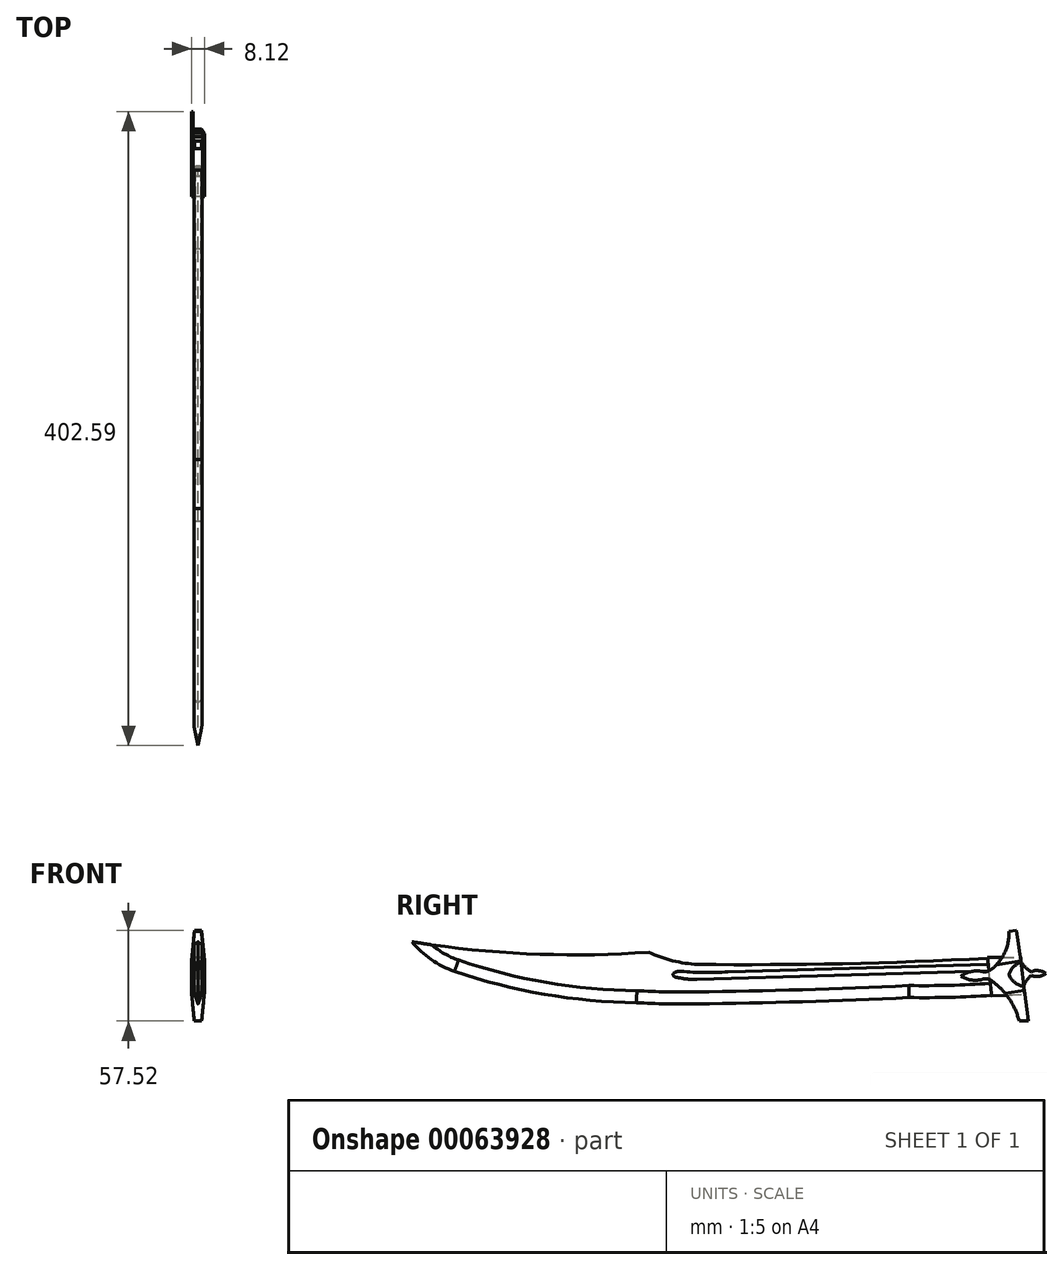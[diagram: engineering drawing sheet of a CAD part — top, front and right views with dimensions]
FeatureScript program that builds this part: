
annotation { "Feature Type Name" : "Feature", "Feature Type Description" : "" }
export const myFeature = defineFeature(function(context is Context, id is Id, definition is map)
    precondition{}
    {
        {
            var Q0;
            Q0=qCreatedBy(makeId("Right.planeOp"),FACE);
            var sketch = newSketch(context, id + "F0", { "sketchPlane" : qUnion([Q0])});
            skArc(sketch, "E0", {"start": v(-222.62, 23.87) * mm, "mid": v(-147.62, 16.22) * mm, "end": v(-72.23, 17.25) * mm});
            skArc(sketch, "E1", {"start": v(-72.23, 17.25) * mm, "mid": v(-57.05, 11.87) * mm, "end": v(-41.12, 9.52) * mm});
            skArc(sketch, "E2", {"start": v(-41.12, 9.52) * mm, "mid": v(50.92, 9.98) * mm, "end": v(142.9, 13.44) * mm});
            skArc(sketch, "E3", {"start": v(-222.62, 23.87) * mm, "mid": v(-210.4, 12.6) * mm, "end": v(-195.6, 5.02) * mm});
            skArc(sketch, "E4", {"start": v(-195.6, 5.02) * mm, "mid": v(-138.62, -9.45) * mm, "end": v(-80.08, -14.85) * mm});
            skLineSegment(sketch, "E5", {"start": v(145.39, -10.22) * mm, "end": v(142.9, 13.44) * mm});
            skArc(sketch, "E6", {"start": v(-80.08, -14.85) * mm, "mid": v(-61.15, -15.54) * mm, "end": v(-42.22, -15.5) * mm});
            skArc(sketch, "E7", {"start": v(-42.22, -15.5) * mm, "mid": v(25.43, -14.14) * mm, "end": v(93.04, -11.56) * mm});
            skArc(sketch, "E8", {"start": v(93.04, -11.56) * mm, "mid": v(119.22, -11.4) * mm, "end": v(145.39, -10.22) * mm});
            skSolve(sketch);
        }
        {
            var Q0;
            Q0 = qSketchRegion(id + "F0", true);
            extrude(context, id + "F1", {"entities" : qUnion([Q0]), "endBound" : BoundingType.SYMMETRIC, "depth" : 5.08 * mm});
        }
        {
            var Q0;
            Q0=qCreatedBy(makeId("Right.planeOp"),FACE);
            var sketch = newSketch(context, id + "F2", { "sketchPlane" : qUnion([Q0])});
            skLineSegment(sketch, "E9.0", {"start": v(145.39, -10.22) * mm, "end": v(142.9, 13.44) * mm});
            skLineSegment(sketch, "E10", {"start": v(143.75, 5.38) * mm, "end": v(-41.72, 0) * mm});
            skLineSegment(sketch, "E11", {"start": v(143.31, 9.5) * mm, "end": v(-22.07, 4.7) * mm});
            skPoint(sketch, "E12", {"position": v(-38, 4.24) * mm});
            skPoint(sketch, "E13.orphan", {"position": v(-55.48, 4.24) * mm});
            skPoint(sketch, "E14.start.orphan", {"position": v(-40.81, 4.24) * mm});
            skArc(sketch, "E15", {"start": v(-51.64, 5.05) * mm, "mid": v(-36.86, 4.37) * mm, "end": v(-22.07, 4.7) * mm});
            skArc(sketch, "E16", {"start": v(-53.43, 1.1) * mm, "mid": v(-47.61, 0.19) * mm, "end": v(-41.72, 0) * mm});
            skLineSegment(sketch, "E17", {"start": v(-52.54, 3.07) * mm, "end": v(-53.43, 1.1) * mm});
            skEllipticalArc(sketch, "E18", {});
            const initialGuessF2  = {"E18": [-0.05253797210752964, 0.0030729959253221716, -1, 0, 0.004336996003985405, 0.0020197694829036552, 4.504185753460669, 1.3625930998708757]};
            skSetInitialGuess(sketch, initialGuessF2);
            skSolve(sketch);
        }
        {
            var Q0;
            Q0=makeQuery(id+"F1.opExtrude","CAP_FACE",FACE,{"disambiguationData":[OSD([sQuery(id+"F0.wireOp",EDGE,"E0"),sQuery(id+"F0.wireOp",EDGE,"E1"),sQuery(id+"F0.wireOp",EDGE,"E2"),sQuery(id+"F0.wireOp",EDGE,"E3"),sQuery(id+"F0.wireOp",EDGE,"E4"),sQuery(id+"F0.wireOp",EDGE,"E5"),sQuery(id+"F0.wireOp",EDGE,"E6"),sQuery(id+"F0.wireOp",EDGE,"E7"),sQuery(id+"F0.wireOp",EDGE,"E8")])],"isStart":false});
            var sketch = newSketch(context, id + "F3", { "sketchPlane" : qUnion([Q0])});
            skEllipticalArc(sketch, "E19.0", {});
            skArc(sketch, "E20.0", {"start": v(-53.43, 1.1) * mm, "mid": v(-47.61, 0.19) * mm, "end": v(-41.72, 0) * mm});
            skLineSegment(sketch, "E21.0", {"start": v(143.75, 5.38) * mm, "end": v(-41.72, 0) * mm});
            skArc(sketch, "E22.0", {"start": v(-51.64, 5.05) * mm, "mid": v(-36.86, 4.37) * mm, "end": v(-22.07, 4.7) * mm});
            skLineSegment(sketch, "E23.0", {"start": v(143.31, 9.5) * mm, "end": v(-22.07, 4.7) * mm});
            skLineSegment(sketch, "E24.0", {"start": v(145.39, -10.22) * mm, "end": v(142.9, 13.44) * mm});
            const initialGuessF3  = {"E19.0": [-0.05253797210752964, 0.0030729959253221716, -1, 0, 0.004336996003985405, 0.0020197694829036552, 4.504185753460669, 1.3625930998708757]};
            skSetInitialGuess(sketch, initialGuessF3);
            skSolve(sketch);
        }
        {
            var Q0;
            Q0 = qSketchRegion(id + "F3", true);
            extrude(context, id + "F4", {"entities" : qUnion([Q0]), "operationType" : NewBodyOperationType.REMOVE, "oppositeDirection" : true, "depth" : 0.76 * mm});
        }
        {
            var Q0;
            Q0=makeQuery(id+"F1.opExtrude","CAP_FACE",FACE,{"disambiguationData":[OSD([sQuery(id+"F0.wireOp",EDGE,"E0"),sQuery(id+"F0.wireOp",EDGE,"E1"),sQuery(id+"F0.wireOp",EDGE,"E2"),sQuery(id+"F0.wireOp",EDGE,"E3"),sQuery(id+"F0.wireOp",EDGE,"E4"),sQuery(id+"F0.wireOp",EDGE,"E5"),sQuery(id+"F0.wireOp",EDGE,"E6"),sQuery(id+"F0.wireOp",EDGE,"E7"),sQuery(id+"F0.wireOp",EDGE,"E8")])],"isStart":true});
            var sketch = newSketch(context, id + "F5", { "sketchPlane" : qUnion([Q0])});
            skArc(sketch, "E25.0", {"start": v(53.43, 1.1) * mm, "mid": v(47.61, 0.19) * mm, "end": v(41.72, 0) * mm});
            skLineSegment(sketch, "E26.0", {"start": v(-143.75, 5.38) * mm, "end": v(41.72, 0) * mm});
            skEllipticalArc(sketch, "E27.0", {});
            skArc(sketch, "E28.0", {"start": v(51.64, 5.05) * mm, "mid": v(36.86, 4.37) * mm, "end": v(22.07, 4.7) * mm});
            skLineSegment(sketch, "E29.0", {"start": v(-143.31, 9.5) * mm, "end": v(22.07, 4.7) * mm});
            skLineSegment(sketch, "E30.0", {"start": v(-145.39, -10.22) * mm, "end": v(-142.9, 13.44) * mm});
            const initialGuessF5  = {"E27.0": [0.05253797210752964, 0.0030729959253221716, 1, 0, 0.004336996003985405, 0.0020197694829036552, 4.920592207308711, 1.7789995537189176]};
            skSetInitialGuess(sketch, initialGuessF5);
            skSolve(sketch);
        }
        {
            var Q0;
            Q0 = qSketchRegion(id + "F5", true);
            extrude(context, id + "F6", {"entities" : qUnion([Q0]), "operationType" : NewBodyOperationType.REMOVE, "oppositeDirection" : true, "depth" : 0.76 * mm});
        }
        {
            var Q0;
            Q0=makeQuery(id+"F1.opExtrude","CAP_EDGE",EDGE,{"disambiguationData":[OSD([sQuery(id+"F0.wireOp",EDGE,"E4")])],"isStart":false});
            var Q1;
            Q1=makeQuery(id+"F1.opExtrude","CAP_EDGE",EDGE,{"disambiguationData":[OSD([sQuery(id+"F0.wireOp",EDGE,"E6")])],"isStart":false});
            var Q2;
            Q2=makeQuery(id+"F1.opExtrude","CAP_EDGE",EDGE,{"disambiguationData":[OSD([sQuery(id+"F0.wireOp",EDGE,"E7")])],"isStart":false});
            var Q3;
            Q3=makeQuery(id+"F1.opExtrude","CAP_EDGE",EDGE,{"disambiguationData":[OSD([sQuery(id+"F0.wireOp",EDGE,"E8")])],"isStart":false});
            var Q4;
            Q4=makeQuery(id+"F1.opExtrude","CAP_EDGE",EDGE,{"disambiguationData":[OSD([sQuery(id+"F0.wireOp",EDGE,"E3")])],"isStart":false});
            chamfer(context, id + "F7", {"entities" : qUnion([Q0, Q1, Q2, Q3, Q4]), "chamferType" : ChamferType.TWO_OFFSETS, "width1" : 7.62 * mm, "oppositeDirection" : false, "width2" : 2.54 * mm, "tangentPropagation" : true});
        }
        {
            var Q0;
            Q0=makeQuery(id+"F1.opExtrude","CAP_EDGE",EDGE,{"disambiguationData":[OSD([sQuery(id+"F0.wireOp",EDGE,"E4")])],"isStart":true});
            var Q1;
            Q1=makeQuery(id+"F1.opExtrude","CAP_EDGE",EDGE,{"disambiguationData":[OSD([sQuery(id+"F0.wireOp",EDGE,"E3")])],"isStart":true});
            var Q2;
            Q2=makeQuery(id+"F1.opExtrude","CAP_EDGE",EDGE,{"disambiguationData":[OSD([sQuery(id+"F0.wireOp",EDGE,"E6")])],"isStart":true});
            var Q3;
            Q3=makeQuery(id+"F1.opExtrude","CAP_EDGE",EDGE,{"disambiguationData":[OSD([sQuery(id+"F0.wireOp",EDGE,"E7")])],"isStart":true});
            var Q4;
            Q4=makeQuery(id+"F1.opExtrude","CAP_EDGE",EDGE,{"disambiguationData":[OSD([sQuery(id+"F0.wireOp",EDGE,"E8")])],"isStart":true});
            chamfer(context, id + "F8", {"entities" : qUnion([Q0, Q1, Q2, Q3, Q4]), "chamferType" : ChamferType.TWO_OFFSETS, "width1" : 2.54 * mm, "oppositeDirection" : false, "width2" : 7.62 * mm, "tangentPropagation" : true});
        }
        {
            var Q0;
            Q0=qCreatedBy(makeId("Right.planeOp"),FACE);
            var sketch = newSketch(context, id + "F9", { "sketchPlane" : qUnion([Q0])});
            skLineSegment(sketch, "E31.0", {"start": v(145.39, -10.22) * mm, "end": v(142.9, 13.44) * mm});
            skLineSegment(sketch, "E32", {"start": v(142.9, 13.44) * mm, "end": v(142.84, 13.99) * mm});
            skLineSegment(sketch, "E33", {"start": v(145.39, -10.22) * mm, "end": v(145.42, -10.53) * mm});
            skLineSegment(sketch, "E34", {"start": v(145.42, -10.53) * mm, "end": v(166.56, -9.44) * mm});
            skLineSegment(sketch, "E35", {"start": v(142.84, 13.99) * mm, "end": v(164.01, 13.99) * mm});
            skLineSegment(sketch, "E36", {"start": v(164.01, 13.99) * mm, "end": v(166.56, -9.44) * mm});
            skSolve(sketch);
        }
        {
            var Q0;
            Q0 = qSketchRegion(id + "F9", true);
            extrude(context, id + "F10", {"entities" : qUnion([Q0]), "endBound" : BoundingType.SYMMETRIC, "depth" : 6.1 * mm});
        }
        {
            var Q0;
            Q0=makeQuery(id+"F10.opExtrude","CAP_EDGE",EDGE,{"disambiguationData":[OSD([sQuery(id+"F9.wireOp",EDGE,"E35")])],"isStart":false});
            var Q1;
            Q1=makeQuery(id+"F10.opExtrude","CAP_EDGE",EDGE,{"disambiguationData":[OSD([sQuery(id+"F9.wireOp",EDGE,"E35")])],"isStart":true});
            var Q2;
            Q2=makeQuery(id+"F10.opExtrude","CAP_EDGE",EDGE,{"disambiguationData":[OSD([sQuery(id+"F9.wireOp",EDGE,"E34")])],"isStart":false});
            var Q3;
            Q3=makeQuery(id+"F10.opExtrude","CAP_EDGE",EDGE,{"disambiguationData":[OSD([sQuery(id+"F9.wireOp",EDGE,"E34")])],"isStart":true});
            fillet(context, id + "F11", {"entities" : qUnion([Q0, Q1, Q2, Q3]), "radius" : 1.78 * mm, "tangentPropagation" : true, "allowEdgeOverflow" : false});
        }
        {
            var Q0;
            Q0=qCreatedBy(makeId("Right.planeOp"),FACE);
            var sketch = newSketch(context, id + "F12", { "sketchPlane" : qUnion([Q0])});
            skArc(sketch, "E37", {"start": v(138.74, 5.21) * mm, "mid": v(141.56, 4.82) * mm, "end": v(144.29, 5.6) * mm});
            skArc(sketch, "E38", {"start": v(138.74, 5.21) * mm, "mid": v(132.09, 4.9) * mm, "end": v(126.06, 2.05) * mm});
            skLineSegment(sketch, "E39.0", {"start": v(145.39, -10.22) * mm, "end": v(142.9, 13.44) * mm});
            skLineSegment(sketch, "E40", {"start": v(155.65, 31.05) * mm, "end": v(161.25, 31.05) * mm});
            skLineSegment(sketch, "E41", {"start": v(161.25, 31.05) * mm, "end": v(164.28, 10.92) * mm});
            skArc(sketch, "E42", {"start": v(164.28, 10.92) * mm, "mid": v(159.47, 7.98) * mm, "end": v(156.53, 3.17) * mm});
            skLineSegment(sketch, "E43", {"start": v(156.53, 3.17) * mm, "end": v(126.06, 2.05) * mm});
            skArc(sketch, "E44.MirrorCS", {"start": v(138.94, -0.18) * mm, "mid": v(132.28, -0.34) * mm, "end": v(126.06, 2.05) * mm});
            skArc(sketch, "E45.MirrorCS", {"start": v(138.94, -0.18) * mm, "mid": v(141.72, 0.43) * mm, "end": v(144.5, -0.15) * mm});
            skArc(sketch, "E46", {"start": v(163.03, -26.47) * mm, "mid": v(156.17, -11.62) * mm, "end": v(144.5, -0.15) * mm});
            skArc(sketch, "E47", {"start": v(156.53, 3.17) * mm, "mid": v(160.14, -1.89) * mm, "end": v(165.82, -4.38) * mm});
            skLineSegment(sketch, "E48", {"start": v(163.03, -26.47) * mm, "end": v(168.8, -26.47) * mm});
            skLineSegment(sketch, "E49", {"start": v(168.8, -26.47) * mm, "end": v(165.82, -4.38) * mm});
            skArc(sketch, "E50", {"start": v(144.29, 5.6) * mm, "mid": v(153.74, 16.72) * mm, "end": v(156.48, 31.05) * mm});
            skSolve(sketch);
        }
        {
            var Q0;
            Q0 = qSketchRegion(id + "F12", true);
            extrude(context, id + "F13", {"entities" : qUnion([Q0]), "endBound" : BoundingType.SYMMETRIC, "depth" : 8.13 * mm});
        }
        {
            var Q0;
            Q0=makeQuery(id+"F13.opExtrude","CAP_EDGE",EDGE,{"disambiguationData":[OSD([sQuery(id+"F12.wireOp",EDGE,"E42")])],"isStart":false});
            var Q1;
            Q1=makeQuery(id+"F13.opExtrude","CAP_EDGE",EDGE,{"disambiguationData":[OSD([sQuery(id+"F12.wireOp",EDGE,"E47")])],"isStart":false});
            var Q2;
            Q2=makeQuery(id+"F13.opExtrude","CAP_EDGE",EDGE,{"disambiguationData":[OSD([sQuery(id+"F12.wireOp",EDGE,"E42")])],"isStart":true});
            var Q3;
            Q3=makeQuery(id+"F13.opExtrude","CAP_EDGE",EDGE,{"disambiguationData":[OSD([sQuery(id+"F12.wireOp",EDGE,"E47")])],"isStart":true});
            fillet(context, id + "F14", {"entities" : qUnion([Q0, Q1, Q2, Q3]), "radius" : 0.76 * mm, "tangentPropagation" : true, "allowEdgeOverflow" : false});
        }
        {
            var Q0;
            Q0=makeQuery(id+"F13.opExtrude","SWEPT_FACE",FACE,{"disambiguationData":[OSD([sQuery(id+"F12.wireOp",EDGE,"E41")])]});
            var sketch = newSketch(context, id + "F15", { "sketchPlane" : qUnion([Q0])});
            skLineSegment(sketch, "E51", {"start": v(-4.06, -12.88) * mm, "end": v(-2.27, 6.7) * mm});
            skPoint(sketch, "E52.start.orphan", {"position": v(0, -25.1) * mm});
            skLineSegment(sketch, "E53", {"start": v(0, -24.7) * mm, "end": v(0, -24.57) * mm});
            skLineSegment(sketch, "E54", {"start": v(0, -24.57) * mm, "end": v(0, -24.7) * mm});
            skLineSegment(sketch, "E55", {"start": v(0, -24.7) * mm, "end": v(-0.45, -24.7) * mm});
            skLineSegment(sketch, "E56", {"start": v(0, -24.57) * mm, "end": v(0, -23.61) * mm});
            skLineSegment(sketch, "E57.MirrorCS", {"start": v(4.06, -12.88) * mm, "end": v(2.27, 6.7) * mm});
            skLineSegment(sketch, "E58", {"start": v(-4.06, -12.88) * mm, "end": v(-14.59, -7) * mm});
            skLineSegment(sketch, "E59", {"start": v(-14.59, -7) * mm, "end": v(-4.7, 7.88) * mm});
            skLineSegment(sketch, "E60", {"start": v(-4.7, 7.88) * mm, "end": v(-2.27, 6.7) * mm});
            skLineSegment(sketch, "E61", {"start": v(2.27, 6.7) * mm, "end": v(6.24, 9.12) * mm});
            skLineSegment(sketch, "E62", {"start": v(6.24, 9.12) * mm, "end": v(7.63, -11.04) * mm});
            skLineSegment(sketch, "E63", {"start": v(7.63, -11.04) * mm, "end": v(4.06, -12.88) * mm});
            skLineSegment(sketch, "E64.0", {"start": v(-4.06, -51.3) * mm, "end": v(4.06, -51.3) * mm});
            skLineSegment(sketch, "E65", {"start": v(0, -51.3) * mm, "end": v(0, 6.7) * mm});
            skPoint(sketch, "E66", {"position": v(0, -22.3) * mm});
            skLineSegment(sketch, "E67", {"start": v(0, -22.3) * mm, "end": v(-2.36, -22.3) * mm});
            skLineSegment(sketch, "E68.MirrorCS", {"start": v(-4.06, -31.71) * mm, "end": v(-2.27, -51.3) * mm});
            skLineSegment(sketch, "E69.MirrorCS", {"start": v(4.06, -31.71) * mm, "end": v(2.27, -51.3) * mm});
            skLineSegment(sketch, "E70.MirrorCS", {"start": v(7.63, -33.56) * mm, "end": v(4.06, -31.71) * mm});
            skLineSegment(sketch, "E71.MirrorCS", {"start": v(6.24, -53.71) * mm, "end": v(7.63, -33.56) * mm});
            skLineSegment(sketch, "E72.MirrorCS", {"start": v(-4.06, -31.71) * mm, "end": v(-14.59, -37.59) * mm});
            skLineSegment(sketch, "E73.MirrorCS", {"start": v(-14.59, -37.59) * mm, "end": v(-4.7, -52.48) * mm});
            skLineSegment(sketch, "E74.MirrorCS", {"start": v(-4.7, -52.48) * mm, "end": v(-2.27, -51.3) * mm});
            skLineSegment(sketch, "E75.MirrorCS", {"start": v(2.27, -51.3) * mm, "end": v(6.24, -53.71) * mm});
            skLineSegment(sketch, "E76", {"start": v(-2.27, 6.7) * mm, "end": v(2.27, 6.7) * mm});
            skLineSegment(sketch, "E77", {"start": v(-2.27, 6.7) * mm, "end": v(-2.27, 10.48) * mm});
            skLineSegment(sketch, "E78", {"start": v(-2.27, 10.48) * mm, "end": v(-4.7, 7.88) * mm});
            skLineSegment(sketch, "E79", {"start": v(2.27, 6.7) * mm, "end": v(2.27, 12.28) * mm});
            skLineSegment(sketch, "E80", {"start": v(2.27, 12.28) * mm, "end": v(6.24, 9.12) * mm});
            skLineSegment(sketch, "E81", {"start": v(-2.27, 10.48) * mm, "end": v(2.27, 12.28) * mm});
            skSolve(sketch);
        }
        {
            var Q0;
            {var subQ0=sQuery(id+"F15.wireOp",EDGE,"E77");Q0=makeQuery(id+"F15.imprint","IMPRINT",FACE,{"disambiguationData":[TD([[makeQuery(id+"F15.imprint","IMPRINT",EDGE,{"derivedFrom":subQ0}),-1.0]])]});}
            var Q1;
            Q1=makeQuery(id+"F15.imprint","IMPRINT",FACE,{"disambiguationData":[TD([[makeQuery(id+"F15.imprint","IMPRINT",EDGE,{"derivedFrom":sQuery(id+"F15.wireOp",EDGE,"E61")}),1.0]])]});
            var Q2;
            Q2=makeQuery(id+"F15.imprint","IMPRINT",FACE,{"disambiguationData":[TD([[makeQuery(id+"F15.imprint","IMPRINT",EDGE,{"derivedFrom":sQuery(id+"F15.wireOp",EDGE,"E60")}),1.0]])]});
            var Q3;
            Q3=makeQuery(id+"F15.imprint","IMPRINT",FACE,{"disambiguationData":[TD([[makeQuery(id+"F15.imprint","IMPRINT",EDGE,{"derivedFrom":sQuery(id+"F15.wireOp",EDGE,"E58")}),-1.0]])]});
            var Q4;
            {var subQ2=sQuery(id+"F15.wireOp",EDGE,"E61");Q4=makeQuery(id+"F15.imprint","IMPRINT",FACE,{"disambiguationData":[TD([[makeQuery(id+"F15.imprint","IMPRINT",EDGE,{"derivedFrom":subQ2}),-1.0]])]});}
            var Q5;
            {var subQ0=sQuery(id+"F15.wireOp",EDGE,"E51");Q5=makeQuery(id+"F15.imprint","IMPRINT",FACE,{"disambiguationData":[TD([[makeQuery(id+"F15.imprint","IMPRINT",EDGE,{"derivedFrom":subQ0}),1.0]])]});}
            var Q6;
            {var subQ0=sQuery(id+"F15.wireOp",EDGE,"E57.MirrorCS");Q6=makeQuery(id+"F15.imprint","IMPRINT",FACE,{"disambiguationData":[TD([[makeQuery(id+"F15.imprint","IMPRINT",EDGE,{"derivedFrom":subQ0}),-1.0]])]});}
            var Q7;
            Q7=makeQuery(id+"F15.imprint","IMPRINT",FACE,{"disambiguationData":[TD([[makeQuery(id+"F15.imprint","IMPRINT",EDGE,{"derivedFrom":sQuery(id+"F15.wireOp",EDGE,"E68.MirrorCS")}),-1.0]])]});
            var Q8;
            Q8=makeQuery(id+"F15.imprint","IMPRINT",FACE,{"disambiguationData":[TD([[makeQuery(id+"F15.imprint","IMPRINT",EDGE,{"derivedFrom":sQuery(id+"F15.wireOp",EDGE,"E69.MirrorCS")}),1.0]])]});
            extrude(context, id + "F16", {"entities" : qUnion([Q0, Q1, Q2, Q3, Q4, Q5, Q6, Q7, Q8]), "operationType" : NewBodyOperationType.REMOVE, "oppositeDirection" : true, "depth" : 25.4 * mm});
        }
        {
            var Q0;
            Q0=makeQuery(id+"F10.opExtrude","CAP_FACE",FACE,{"disambiguationData":[OSD([sQuery(id+"F9.wireOp",EDGE,"E31.0"),sQuery(id+"F9.wireOp",EDGE,"E32"),sQuery(id+"F9.wireOp",EDGE,"E33"),sQuery(id+"F9.wireOp",EDGE,"E34"),sQuery(id+"F9.wireOp",EDGE,"E35"),sQuery(id+"F9.wireOp",EDGE,"E36")])],"isStart":true});
            var sketch = newSketch(context, id + "F17", { "sketchPlane" : qUnion([Q0])});
            skArc(sketch, "E82.0", {"start": v(-156.53, 3.17) * mm, "mid": v(-159.47, 7.98) * mm, "end": v(-164.28, 10.92) * mm});
            skArc(sketch, "E83.0", {"start": v(-165.82, -4.38) * mm, "mid": v(-160.14, -1.89) * mm, "end": v(-156.53, 3.17) * mm});
            skArc(sketch, "E84", {"start": v(-170.7, 4.91) * mm, "mid": v(-167.13, 7.53) * mm, "end": v(-164.28, 10.92) * mm});
            skArc(sketch, "E85", {"start": v(-165.82, -4.38) * mm, "mid": v(-167.8, -0.63) * mm, "end": v(-170.7, 2.46) * mm});
            skLineSegment(sketch, "E86", {"start": v(-170.7, 2.46) * mm, "end": v(-170.7, 4.91) * mm});
            skLineSegment(sketch, "E87", {"start": v(-170.7, 3.68) * mm, "end": v(-179.97, 3.68) * mm});
            skPoint(sketch, "E88.start.orphan", {"position": v(-179.97, 3.31) * mm});
            skArc(sketch, "E89", {"start": v(-170.7, 4.91) * mm, "mid": v(-175.5, 5.54) * mm, "end": v(-179.97, 3.68) * mm});
            skArc(sketch, "E90", {"start": v(-179.97, 3.68) * mm, "mid": v(-175.5, 1.83) * mm, "end": v(-170.7, 2.46) * mm});
            skSolve(sketch);
        }
        {
            var Q0;
            Q0 = qSketchRegion(id + "F17", true);
            extrude(context, id + "F18", {"entities" : qUnion([Q0]), "depth" : 1.02 * mm});
        }
    });
